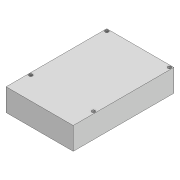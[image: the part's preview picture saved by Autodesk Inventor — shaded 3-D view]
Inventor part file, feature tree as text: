
AUTODESK INVENTOR PART (.ipt)
format: ipt  version: 2020 (Build 240168000, 168)  size: 108,032 bytes
history: native  units: mm
features: sketch x2, extrude x1, hole x1
ambient origin geometry x8: Origin, YZ Plane, XZ Plane, XY Plane, X Axis, Y Axis, Z Axis, Center Point
bodies: Volumenkörper1 (feature_tree)
feature tree (4):
  extrude  "Extrusion1"  Depth=90.0mm
  hole  "Bohrung1"  [1 undecoded]
  sketch  "Skizze1"  dims[d0=60.0mm d1=90.0mm]
  sketch  "Skizze2"  dims[d2=20.0mm d3=0.0mm d4=2.0mm d5=2.0mm d6=2.0mm d7=2.0mm d8=2.0mm d9=2.0mm d10=20.0mm d11=20.0mm d12=3.0mm d13=6.0mm d14=4.0mm d15=2.0mm d16=90.0deg d17=8.0mm d18=20.594885mm]
note: 1 required parameter value undecoded (feature->parameter linkage not recoverable at this tier; creation-order binding heuristic only, values carry confidence <= 0.55)
